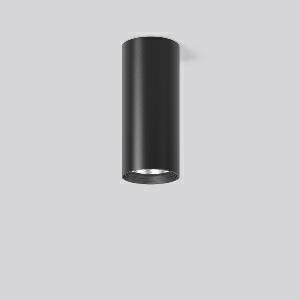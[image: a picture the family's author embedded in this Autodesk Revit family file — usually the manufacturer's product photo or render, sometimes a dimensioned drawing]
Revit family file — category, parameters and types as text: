
# Revit family: heledon_mini_a_931201_003_3_37cb
name_source: partatom
category: Lighting Fixtures
units: mm (PartAtom-declared; Revit-internal decimal feet)

## family parameters
Cut with Voids When Loaded = No
Host = Face
Light Source = No
Part Type = Normal
Room Calculation Point = No
Round Connector Dimension = Use Diameter
Shared = No

## types (1)
- HELEDON mini A (1 x LED Modul 935, 2500 lm, 3500)
    Apparent Load = 20 VA
    Approval mark = CE
    CIE Flux Codes = 99 100 100 100 100
    Color Rendering = 92
    Color Temperature = 3500
    Default Elevation = 1800 mm
    Description = Series: HELEDON mini
Cylindrical surface-mounted downlight. Housing: die-cast aluminium, powder-coated. Internal ceiling frame polycarbonate with bayonet mounting. Black plastic ring and recessed LED to prevent glare from the side. Optical assembly with reflector made of MIRO-Silver with 98% total light reflection for outstanding efficiency - can be changed without tools. Best colour rendering index Ra>90. Suitable for Ceiling mounting. Easy installation with a separate ceiling frame with bayonet mounting and plug connection. Driver integrated. Connected via plug-in connector. High quality converter without flickering and stroboscopic effect. The following accessories can be mounted without use of tools: interchangeable lenses, decorative glasses, honeycomb louvre, clear and frosted diffusers, white interchangeable plastic ring. 
Colour: deep black, matt (RAL 9005)
Diameter: 87 mm
Height: 197 mm
Lamp: LED
Socket: without socket
Colour temperature: 3500K
Colour rendering index (CRI): 92
System power: 20 W
Rated luminous flux: 2500 lm
Luminous efficiency: 125 lm/W
Control gear: Regulated power supply
Protection class: I
Type of protection: IP 20
    Height = 197 mm
    Lamp = 1 x LED Modul 935
    Lamp Light Flux = 2500 lm
    Lamp count = 1
    Length = 87 mm
    Lifetime = 50000 h
    Luminous efficacy = 125 lm/W
    Manufacturer = RZB
    ModVariant = No
    Model = 931201.003.3
    Mounting Place = Ceiling
    Mounting Type = Surface mounted
    Number of Poles = 1
    OnlyDefault = Yes
    Power Factor = 1
    Product Name = HELEDON mini A
    Product group = Surface mounted downlights
    ProductGroupID = 302
    Protection Class = Protection class I
    Protection Degree = IP 20
    RLX_Detail_Level = 1
    RLX_Emergency_Light_Flux = 0 lm
    RLX_Emergency_Type = 0
    RLX_Emergency_Type_DB = No
    RlxData = <blob elided: 106957 chars, md5=2ea286d9>
    Socket = socket
    Standby Power = 0 W
    System Light Flux = 2500 lm
    System Power = 20 W
    Type Comments = Product without accessories
    Type Image = 931188.003.jpg
    URL = http://relux.com
    VarID = ---
    Voltage = 230 V
    Voltage Range = 220-240 V
    Weight = 0.00 kg
    Width = 0 mm  [stored 0 ft]

note: [stored X ft] marks values corroborated as IEEE doubles in the binary element streams (Revit-internal decimal feet)

## geometry (parser evidence)
native form markers: Blend x4, Sweep x10
no freeform markers — native parametric forms only
